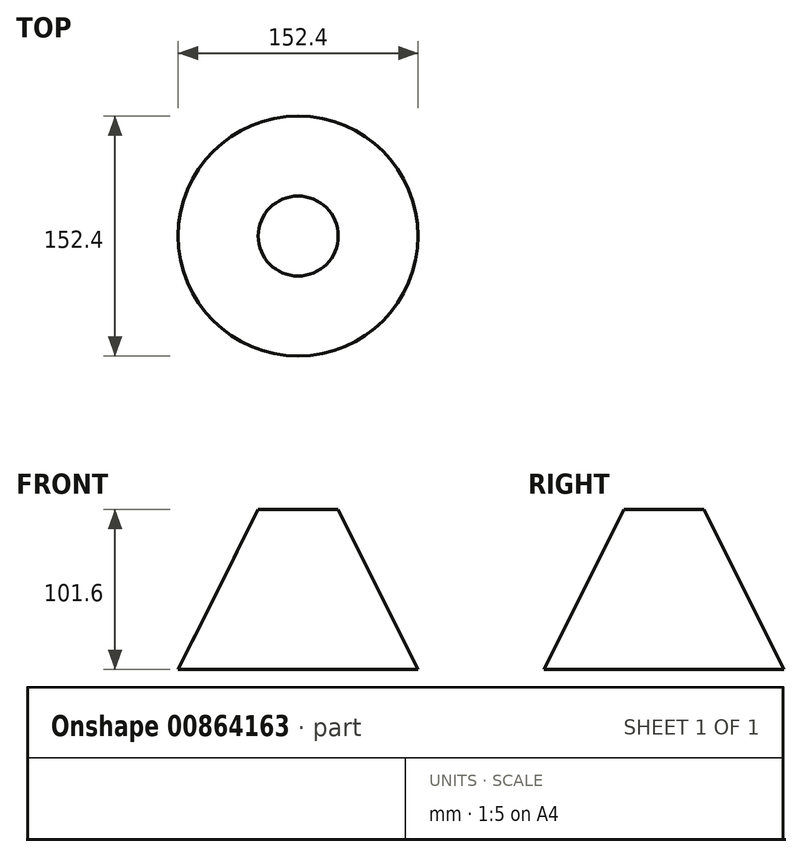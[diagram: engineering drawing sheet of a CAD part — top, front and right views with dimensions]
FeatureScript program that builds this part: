
annotation { "Feature Type Name" : "Feature", "Feature Type Description" : "" }
export const myFeature = defineFeature(function(context is Context, id is Id, definition is map)
    precondition{}
    {
        {
            var Q0;
            Q0=qCreatedBy(makeId("Front.planeOp"),FACE);
            var sketch = newSketch(context, id + "F0", { "sketchPlane" : qUnion([Q0])});
            skLineSegment(sketch, "E0", {"start": v(0, 0) * mm, "end": v(0, 101.6) * mm});
            skLineSegment(sketch, "E1", {"start": v(0, 101.6) * mm, "end": v(-25.4, 101.6) * mm});
            skLineSegment(sketch, "E2", {"start": v(-25.4, 101.6) * mm, "end": v(-76.2, 0) * mm});
            skLineSegment(sketch, "E3", {"start": v(-76.2, 0) * mm, "end": v(0, 0) * mm});
            skSolve(sketch);
        }
        {
            var Q0;
            Q0=makeQuery(id+"F0.imprint","IMPRINT",FACE,{"disambiguationData":[TD([[makeQuery(id+"F0.imprint","IMPRINT",EDGE,{"derivedFrom":sQuery(id+"F0.wireOp",EDGE,"E0")}),1.0]])]});
            var Q1;
            Q1=sQuery(id+"F0.wireOp",EDGE,"E0");
            revolve(context, id + "F1", {"surfaceOperationType" : NewSurfaceOperationType.NEW, "entities" : qUnion([Q0]), "axis" : qUnion([Q1]), "revolveType" : RevolveType.FULL});
        }
    });
